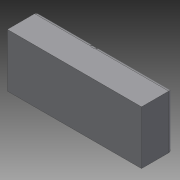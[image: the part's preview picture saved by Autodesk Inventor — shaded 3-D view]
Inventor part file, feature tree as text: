
AUTODESK INVENTOR PART (.ipt)
format: ipt  version: 2014 (Build 180170000, 170)  size: 130,560 bytes
history: native  units: mm
features: extrude x3, fillet x3, sketch x3
ambient origin geometry x8: Origin, YZ Plane, XZ Plane, XY Plane, X Axis, Y Axis, Z Axis, Center Point
bodies: Volumenkörper1 (feature_tree)
feature tree (9):
  extrude  "Extrusion1"  Depth=2.75mm
  extrude  "Extrusion2"  Depth=1.6mm
  extrude  "Extrusion3"  Depth=0.2mm
  fillet  "Rundung2"  Radius=3.0mm
  fillet  "Rundung3"  Radius=2.48mm
  fillet  "Rundung4"  Radius=0.1mm
  sketch  "Skizze1"  dims[d0=6.9mm d1=2.75mm]
  sketch  "Skizze2"  dims[d2=1.6mm d3=0.0mm d4=1.8mm]
  sketch  "Skizze7"  dims[d5=2.0mm d6=3.88mm d7=3.0mm d8=2.48mm d9=0.1mm d10=0.0mm d18=2.48mm d19=0.1mm d20=0.1mm d21=0.2mm d22=0.0mm d23=0.2mm d24=0.2mm d25=0.2mm]
